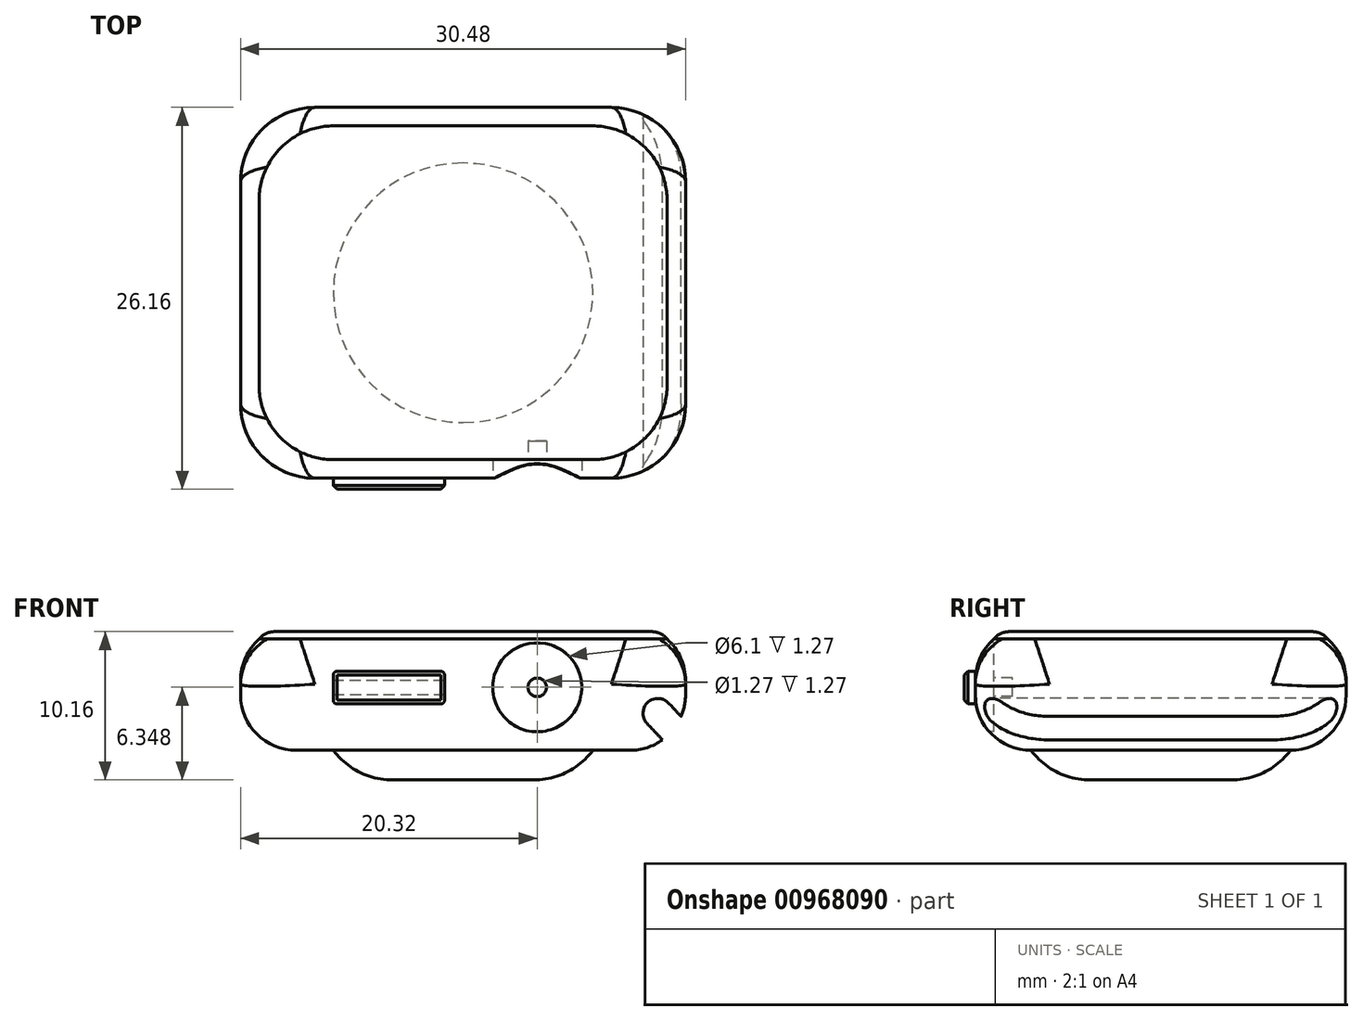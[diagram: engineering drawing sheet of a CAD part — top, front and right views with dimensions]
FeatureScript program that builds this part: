
annotation { "Feature Type Name" : "Feature", "Feature Type Description" : "" }
export const myFeature = defineFeature(function(context is Context, id is Id, definition is map)
    precondition{}
    {
        {
            var Q0;
            Q0=qCreatedBy(makeId("Top.planeOp"),FACE);
            var sketch = newSketch(context, id + "F0", { "sketchPlane" : qUnion([Q0])});
            skLineSegment(sketch, "E0.bottom", {"start": v(-13.97, -11.43) * mm, "end": v(13.97, -11.43) * mm});
            skLineSegment(sketch, "E0.top", {"start": v(-13.97, 11.43) * mm, "end": v(13.97, 11.43) * mm});
            skLineSegment(sketch, "E0.left", {"start": v(-13.97, -11.43) * mm, "end": v(-13.97, 11.43) * mm});
            skLineSegment(sketch, "E0.right", {"start": v(13.97, -11.43) * mm, "end": v(13.97, 11.43) * mm});
            skPoint(sketch, "E0.middle", {"position": v(0, 0) * mm});
            skLineSegment(sketch, "E1.bottom", {"start": v(-15.24, -12.7) * mm, "end": v(15.24, -12.7) * mm});
            skLineSegment(sketch, "E1.top", {"start": v(-15.24, 12.7) * mm, "end": v(15.24, 12.7) * mm});
            skLineSegment(sketch, "E1.left", {"start": v(-15.24, -12.7) * mm, "end": v(-15.24, 12.7) * mm});
            skLineSegment(sketch, "E1.right", {"start": v(15.24, -12.7) * mm, "end": v(15.24, 12.7) * mm});
            skSolve(sketch);
        }
        {
            var Q0;
            Q0=makeQuery(id+"F0.imprint","IMPRINT",FACE,{"disambiguationData":[TD([[makeQuery(id+"F0.imprint","IMPRINT",EDGE,{"derivedFrom":sQuery(id+"F0.wireOp",EDGE,"E0.bottom")}),1.0]])]});
            var Q1;
            Q1=makeQuery(id+"F0.imprint","IMPRINT",FACE,{"disambiguationData":[TD([[makeQuery(id+"F0.imprint","IMPRINT",EDGE,{"derivedFrom":sQuery(id+"F0.wireOp",EDGE,"E0.bottom")}),-1.0]])]});
            extrude(context, id + "F1", {"entities" : qUnion([Q0, Q1]), "depth" : 7.62 * mm, "offsetDistance" : 25.4 * mm});
        }
        {
            var Q0;
            Q0=makeQuery(id+"F0.imprint","IMPRINT",FACE,{"disambiguationData":[TD([[makeQuery(id+"F0.imprint","IMPRINT",EDGE,{"derivedFrom":sQuery(id+"F0.wireOp",EDGE,"E0.bottom")}),1.0]])]});
            extrude(context, id + "F2", {"entities" : qUnion([Q0]), "operationType" : NewBodyOperationType.ADD, "depth" : 8.13 * mm, "offsetDistance" : 25.4 * mm});
        }
        {
            var Q0;
            Q0=makeQuery(id+"F2.opExtrude","SWEPT_EDGE",EDGE,{"disambiguationData":[OSD([sQuery(id+"F0.wireOp",EDGE,"E0.bottom"),sQuery(id+"F0.wireOp",EDGE,"E0.right")])]});
            var Q1;
            Q1=makeQuery(id+"F2.opExtrude","SWEPT_EDGE",EDGE,{"disambiguationData":[OSD([sQuery(id+"F0.wireOp",EDGE,"E0.bottom"),sQuery(id+"F0.wireOp",EDGE,"E0.left")])]});
            var Q2;
            Q2=makeQuery(id+"F2.opExtrude","SWEPT_EDGE",EDGE,{"disambiguationData":[OSD([sQuery(id+"F0.wireOp",EDGE,"E0.top"),sQuery(id+"F0.wireOp",EDGE,"E0.right")])]});
            var Q3;
            Q3=makeQuery(id+"F2.opExtrude","SWEPT_EDGE",EDGE,{"disambiguationData":[OSD([sQuery(id+"F0.wireOp",EDGE,"E0.top"),sQuery(id+"F0.wireOp",EDGE,"E0.left")])]});
            fillet(context, id + "F3", {"entities" : qUnion([Q0, Q1, Q2, Q3]), "radius" : 5.08 * mm, "tangentPropagation" : true, "allowEdgeOverflow" : false});
        }
        {
            var Q0;
            Q0=makeQuery(id+"F1.opExtrude","SWEPT_EDGE",EDGE,{"disambiguationData":[OSD([sQuery(id+"F0.wireOp",EDGE,"E1.top"),sQuery(id+"F0.wireOp",EDGE,"E1.right")])]});
            var Q1;
            Q1=makeQuery(id+"F1.opExtrude","SWEPT_EDGE",EDGE,{"disambiguationData":[OSD([sQuery(id+"F0.wireOp",EDGE,"E1.bottom"),sQuery(id+"F0.wireOp",EDGE,"E1.right")])]});
            var Q2;
            Q2=makeQuery(id+"F1.opExtrude","SWEPT_EDGE",EDGE,{"disambiguationData":[OSD([sQuery(id+"F0.wireOp",EDGE,"E1.top"),sQuery(id+"F0.wireOp",EDGE,"E1.left")])]});
            var Q3;
            Q3=makeQuery(id+"F1.opExtrude","SWEPT_EDGE",EDGE,{"disambiguationData":[OSD([sQuery(id+"F0.wireOp",EDGE,"E1.bottom"),sQuery(id+"F0.wireOp",EDGE,"E1.left")])]});
            fillet(context, id + "F4", {"entities" : qUnion([Q0, Q1, Q2, Q3]), "radius" : 5.08 * mm, "tangentPropagation" : true, "allowEdgeOverflow" : false});
        }
        {
            var Q0;
            Q0=makeQuery(id+"F1.opExtrude","CAP_EDGE",EDGE,{"disambiguationData":[OSD([sQuery(id+"F0.wireOp",EDGE,"E1.bottom")])],"isStart":false});
            var Q1;
            Q1=makeQuery(id+"F1.opExtrude","CAP_EDGE",EDGE,{"disambiguationData":[OSD([sQuery(id+"F0.wireOp",EDGE,"E1.bottom")])],"isStart":true});
            fillet(context, id + "F5", {"entities" : qUnion([Q0, Q1]), "radius" : 3.8 * mm, "tangentPropagation" : true, "allowEdgeOverflow" : false});
        }
        {
            var Q0;
            Q0=makeQuery(id+"F2.opExtrude","CAP_EDGE",EDGE,{"disambiguationData":[OSD([sQuery(id+"F0.wireOp",EDGE,"E0.bottom")])],"isStart":false});
            fillet(context, id + "F6", {"entities" : qUnion([Q0]), "radius" : 1.27 * mm, "tangentPropagation" : true, "allowEdgeOverflow" : false});
        }
        {
            var Q0;
            Q0=makeQuery(id+"F1.opExtrude","SWEPT_FACE",FACE,{"disambiguationData":[OSD([sQuery(id+"F0.wireOp",EDGE,"E1.bottom")])]});
            var sketch = newSketch(context, id + "F7", { "sketchPlane" : qUnion([Q0])});
            skCircle(sketch, "E2", {"center": v(5.08, 4.32) * mm, "radius": 0.64 * mm});
            skSolve(sketch);
        }
        {
            var Q0;
            Q0 = qSketchRegion(id + "F7", true);
            var Q1;
            {var subQ0=sQuery(id+"F7.wireOp",EDGE,"E2");var subQ1=sQuery(id+"F0.wireOp",EDGE,"E1.bottom");var subQ2=makeQuery(id+"F1.opExtrude","SWEPT_FACE",FACE,{"disambiguationData":[OSD([subQ1])]});var subQ3=makeQuery(id+"F5.opFillet","BLEND_EDGE",EDGE,{"disambiguationData":[OD(1.0)],"blendedFrom":[makeQuery(id+"F1.opExtrude","CAP_EDGE",EDGE,{"disambiguationData":[OSD([subQ1])],"isStart":false}),subQ2],"blendedInto":[subQ2]});var subQ4=makeQuery(id+"F7.imprint","INTERSECT",VERTEX,{"disambiguationData":[OD(0.0)],"derivedFrom":[subQ3,subQ0]});Q1=makeQuery(id+"F7.imprint","IMPRINT",FACE,{"disambiguationData":[TD([[makeQuery(id+"F7.imprint","IMPRINT",EDGE,{"disambiguationData":[TD([[subQ4,-1.0]])],"derivedFrom":subQ0}),1.0]])]});}
            extrude(context, id + "F8", {"entities" : qUnion([Q0, Q1]), "operationType" : NewBodyOperationType.REMOVE, "oppositeDirection" : true, "depth" : 2.54 * mm, "offsetDistance" : 25.4 * mm});
        }
        {
            var Q0;
            {var subQ3=sQuery(id+"F0.wireOp",EDGE,"E1.bottom");var subQ5=makeQuery(id+"F1.opExtrude","CAP_EDGE",EDGE,{"disambiguationData":[OSD([subQ3])],"isStart":false});Q0=makeQuery(id+"F8.boolean.opBoolean","SPLIT",FACE,{"disambiguationData":[TD([makeQuery(id+"F5.opFillet","BLEND_FACE",FACE,{"disambiguationData":[OSD([subQ3]),TDD([subQ5]),OD(0.0)]})])],"derivedFrom":makeQuery(id+"F1.opExtrude","SWEPT_FACE",FACE,{"disambiguationData":[OSD([subQ3])]})});}
            var sketch = newSketch(context, id + "F9", { "sketchPlane" : qUnion([Q0])});
            skLineSegment(sketch, "E3.bottom", {"start": v(-8.9, 5.42) * mm, "end": v(-1.27, 5.42) * mm});
            skLineSegment(sketch, "E3.top", {"start": v(-8.9, 3.17) * mm, "end": v(-1.27, 3.17) * mm});
            skLineSegment(sketch, "E3.left", {"start": v(-8.9, 5.42) * mm, "end": v(-8.9, 3.17) * mm});
            skLineSegment(sketch, "E3.right", {"start": v(-1.27, 5.42) * mm, "end": v(-1.27, 3.17) * mm});
            skSolve(sketch);
        }
        {
            var Q0;
            Q0 = qSketchRegion(id + "F9", true);
            extrude(context, id + "F10", {"entities" : qUnion([Q0]), "operationType" : NewBodyOperationType.ADD, "depth" : 0.76 * mm, "offsetDistance" : 25.4 * mm});
        }
        {
            var Q0;
            Q0=qCreatedBy(makeId("Front.planeOp"),FACE);
            var sketch = newSketch(context, id + "F11", { "sketchPlane" : qUnion([Q0])});
            skCircle(sketch, "E4", {"center": v(13.34, 2.54) * mm, "radius": 1.02 * mm});
            skLineSegment(sketch, "E5", {"start": v(12.6, 1.84) * mm, "end": v(14.34, 0) * mm});
            skLineSegment(sketch, "E6", {"start": v(14.34, 0) * mm, "end": v(15.82, 1.4) * mm});
            skLineSegment(sketch, "E7", {"start": v(15.82, 1.4) * mm, "end": v(14.07, 3.24) * mm});
            skSolve(sketch);
        }
        {
            var Q0;
            Q0 = qSketchRegion(id + "F11", true);
            extrude(context, id + "F12", {"entities" : qUnion([Q0]), "operationType" : NewBodyOperationType.REMOVE, "oppositeDirection" : true, "depth" : 50.8 * mm, "offsetDistance" : 25.4 * mm, "hasSecondDirection" : true, "secondDirectionOppositeDirection" : false, "secondDirectionDepth" : 50.8 * mm});
        }
        {
            var Q0;
            Q0=makeQuery(id+"F1.opExtrude","CAP_FACE",FACE,{"disambiguationData":[OSD([sQuery(id+"F0.wireOp",EDGE,"E1.bottom"),sQuery(id+"F0.wireOp",EDGE,"E1.top"),sQuery(id+"F0.wireOp",EDGE,"E1.left"),sQuery(id+"F0.wireOp",EDGE,"E1.right")])],"isStart":true});
            var sketch = newSketch(context, id + "F13", { "sketchPlane" : qUnion([Q0])});
            skCircle(sketch, "E8", {"center": v(0, 0) * mm, "radius": 8.89 * mm});
            skSolve(sketch);
        }
        {
            var Q0;
            Q0 = qSketchRegion(id + "F13", true);
            extrude(context, id + "F14", {"entities" : qUnion([Q0]), "operationType" : NewBodyOperationType.ADD, "depth" : 2.03 * mm, "offsetDistance" : 25.4 * mm});
        }
        {
            var Q0;
            Q0=makeQuery(id+"F14.opExtrude","CAP_EDGE",EDGE,{"disambiguationData":[OSD([sQuery(id+"F13.wireOp",EDGE,"E8")])],"isStart":false});
            fillet(context, id + "F15", {"entities" : qUnion([Q0]), "radius" : 5.08 * mm, "tangentPropagation" : true, "allowEdgeOverflow" : false});
        }
        {
            var Q0;
            {var subQ0=makeQuery(id+"F8.opExtrude","SWEPT_FACE",FACE,{"disambiguationData":[OSD([sQuery(id+"F7.wireOp",EDGE,"E2")])]});var subQ1=sQuery(id+"F0.wireOp",EDGE,"E1.bottom");var subQ2=makeQuery(id+"F1.opExtrude","CAP_EDGE",EDGE,{"disambiguationData":[OSD([subQ1])],"isStart":false});Q0=makeQuery(id+"F10.boolean.opBoolean","SPLIT",FACE,{"disambiguationData":[TD([makeQuery(id+"F8.boolean.opBoolean","COPY",FACE,{"derivedFrom":subQ0})])],"derivedFrom":makeQuery(id+"F8.boolean.opBoolean","SPLIT",FACE,{"disambiguationData":[TD([makeQuery(id+"F5.opFillet","BLEND_FACE",FACE,{"disambiguationData":[OSD([subQ1]),TDD([subQ2]),OD(0.0)]})])],"derivedFrom":makeQuery(id+"F1.opExtrude","SWEPT_FACE",FACE,{"disambiguationData":[OSD([subQ1])]})})});}
            var sketch = newSketch(context, id + "F16", { "sketchPlane" : qUnion([Q0])});
            skCircle(sketch, "E9", {"center": v(5.08, 4.32) * mm, "radius": 3.05 * mm});
            skSolve(sketch);
        }
        {
            var Q0;
            Q0 = qSketchRegion(id + "F16", true);
            extrude(context, id + "F17", {"entities" : qUnion([Q0]), "operationType" : NewBodyOperationType.REMOVE, "oppositeDirection" : true, "depth" : 1.27 * mm, "offsetDistance" : 25.4 * mm});
        }
        {
            var Q0;
            Q0=makeQuery(id+"F10.opExtrude","SWEPT_EDGE",EDGE,{"disambiguationData":[OSD([sQuery(id+"F9.wireOp",EDGE,"E3.bottom"),sQuery(id+"F9.wireOp",EDGE,"E3.right")])]});
            var Q1;
            Q1=makeQuery(id+"F10.opExtrude","SWEPT_EDGE",EDGE,{"disambiguationData":[OSD([sQuery(id+"F9.wireOp",EDGE,"E3.bottom"),sQuery(id+"F9.wireOp",EDGE,"E3.left")])]});
            var Q2;
            Q2=makeQuery(id+"F10.opExtrude","SWEPT_EDGE",EDGE,{"disambiguationData":[OSD([sQuery(id+"F9.wireOp",EDGE,"E3.top"),sQuery(id+"F9.wireOp",EDGE,"E3.left")])]});
            var Q3;
            Q3=makeQuery(id+"F10.opExtrude","SWEPT_EDGE",EDGE,{"disambiguationData":[OSD([sQuery(id+"F9.wireOp",EDGE,"E3.top"),sQuery(id+"F9.wireOp",EDGE,"E3.right")])]});
            fillet(context, id + "F18", {"entities" : qUnion([Q0, Q1, Q2, Q3]), "radius" : 0.25 * mm, "tangentPropagation" : true, "allowEdgeOverflow" : false});
        }
        {
            var Q0;
            Q0=makeQuery(id+"F10.opExtrude","CAP_EDGE",EDGE,{"disambiguationData":[OSD([sQuery(id+"F9.wireOp",EDGE,"E3.top")])],"isStart":false});
            var Q1;
            Q1=makeQuery(id+"F10.opExtrude","CAP_EDGE",EDGE,{"disambiguationData":[OSD([sQuery(id+"F9.wireOp",EDGE,"E3.right")])],"isStart":false});
            var Q2;
            Q2=makeQuery(id+"F10.opExtrude","CAP_EDGE",EDGE,{"disambiguationData":[OSD([sQuery(id+"F9.wireOp",EDGE,"E3.bottom")])],"isStart":false});
            var Q3;
            Q3=makeQuery(id+"F10.opExtrude","CAP_EDGE",EDGE,{"disambiguationData":[OSD([sQuery(id+"F9.wireOp",EDGE,"E3.left")])],"isStart":false});
            chamfer(context, id + "F19", {"entities" : qUnion([Q0, Q1, Q2, Q3]), "width" : 0.25 * mm, "tangentPropagation" : true});
        }
    });
